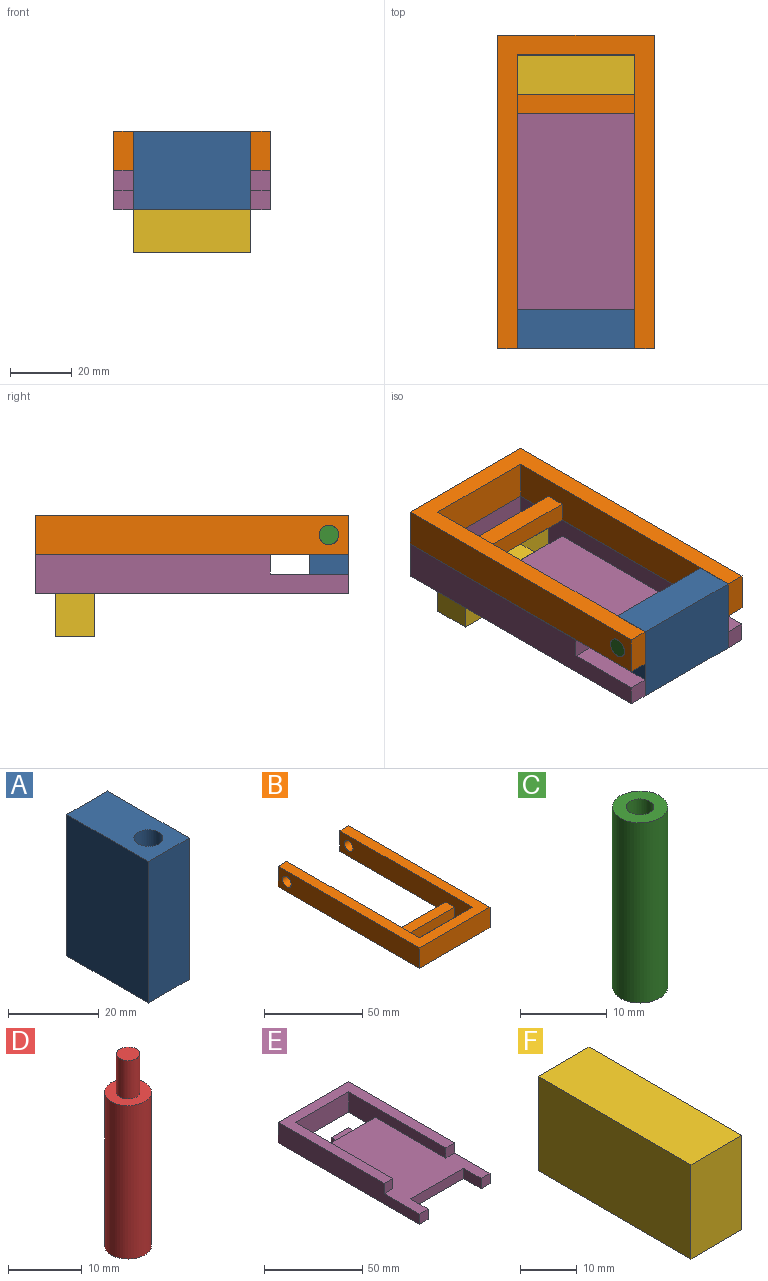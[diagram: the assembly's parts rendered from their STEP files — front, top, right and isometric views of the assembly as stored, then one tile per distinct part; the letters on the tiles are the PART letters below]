
ASSEMBLY  parts=6 mates=5
PART A: 7 faces, bbox 12.7x25.4x38.1 mm
  f0: plane 25.4x12.7mm, normal (0,0,-1), area 290.9mm2, adj f1,f3,f4,f5,f6
  f1: plane 38.1x25.4mm, normal (-1,0,0), area 967.7mm2, adj f0,f2,f4,f5
  f2: plane 25.4x12.7mm, normal (0,0,1), area 290.9mm2, adj f1,f3,f4,f5,f6
  f3: plane 38.1x25.4mm, normal (1,0,0), area 967.7mm2, adj f0,f2,f4,f5
  f4: plane 38.1x12.7mm, normal (0,1,0), area 483.9mm2, adj f0,f1,f2,f3
  f5: plane 38.1x12.7mm, normal (0,-1,0), area 483.9mm2, adj f0,f1,f2,f3
  f6: cylinder r=3.17mm len=38.1mm, axis (0,0,1), area 760.1mm2, adj f0,f2
PART B: 15 faces, bbox 50.8x101.6x12.7 mm
  f0: plane 95.25x12.7mm, normal (-1,0,0), area 1137.7mm2, adj f1,f7,f8,f9,f11,f12,f13,f14
  f1: plane 12.7x6.35mm, normal (0,1,0), area 80.6mm2, adj f0,f2,f8,f9
  f2: plane 101.6x12.7mm, normal (1,0,0), area 1258.7mm2, adj f1,f3,f8,f9,f11
  f3: plane 50.8x12.7mm, normal (0,-1,0), area 645.2mm2, adj f2,f4,f8,f9
  f4: plane 101.6x12.7mm, normal (-1,0,0), area 1258.7mm2, adj f3,f5,f8,f9,f10
  f5: plane 12.7x6.35mm, normal (0,1,0), area 80.6mm2, adj f4,f6,f8,f9
  f6: plane 95.25x12.7mm, normal (1,0,0), area 1137.7mm2, adj f5,f7,f8,f9,f10,f12,f13,f14
  f7: plane 38.1x12.7mm, normal (0,1,0), area 483.9mm2, adj f0,f6,f8,f9
  f8: plane 101.6x50.8mm, normal (0,0,-1), area 1774.2mm2, adj f0,f1,f2,f3,f4,f5,f6,f7
  f9: plane 101.6x50.8mm, normal (0,0,1), area 1532.3mm2, adj f0,f1,f2,f3,f4,f5,f6,f7
  f10: cylinder r=3.17mm len=6.35mm, axis (1,0,0), area 126.7mm2, adj f4,f6
  f11: cylinder r=3.17mm len=6.35mm, axis (1,0,0), area 126.7mm2, adj f0,f2
  f12: plane 38.1x6.35mm, normal (0,0,1), area 241.9mm2, adj f0,f6,f13,f14
  f13: plane 38.1x6.35mm, normal (0,1,0), area 241.9mm2, adj f0,f6,f8,f12
  f14: plane 38.1x6.35mm, normal (0,-1,0), area 241.9mm2, adj f0,f6,f8,f12
PART C: 5 faces, bbox 6.4x6.4x25.4 mm
  f0: cylinder r=3.17mm len=25.4mm, axis (0,0,-1), area 506.7mm2, adj f1,f2
  f1: plane 6.35x6.35mm, normal (0,0,1), area 23.8mm2, adj f0,f3
  f2: plane 6.35x6.35mm, normal (0,0,-1), area 31.7mm2, adj f0
  f3: cylinder r=1.59mm len=6.35mm, axis (0,0,1), area 63.3mm2, adj f1,f4
  f4: plane 3.18x3.18mm, normal (0,0,1), area 7.9mm2, adj f3
PART D: 5 faces, bbox 6.4x6.4x31.8 mm
  f0: cylinder r=3.17mm len=25.4mm, axis (0,0,-1), area 506.7mm2, adj f1,f2
  f1: plane 6.35x6.35mm, normal (0,0,1), area 23.8mm2, adj f0,f3
  f2: plane 6.35x6.35mm, normal (0,0,-1), area 31.7mm2, adj f0
  f3: cylinder r=1.59mm len=6.35mm, axis (0,0,-1), area 63.3mm2, adj f1,f4
  f4: plane 3.18x3.18mm, normal (0,0,1), area 7.9mm2, adj f3
PART E: 21 faces, bbox 50.8x101.6x12.7 mm
  f0: plane 12.7x3.18mm, normal (0,1,0), area 40.3mm2, adj f1,f2,f19,f20
  f1: plane 12.7x6.35mm, normal (0,0,1), area 80.6mm2, adj f0,f18,f19,f20
  f2: plane 101.6x50.8mm, normal (0,0,-1), area 4032.3mm2, adj f0,f3,f5,f6,f7,f8,f10,f11
  f3: plane 6.35x6.35mm, normal (0,-1,0), area 40.3mm2, adj f2,f7,f14,f16
  f4: plane 76.2x50.8mm, normal (0,0,1), area 1209.7mm2, adj f5,f7,f8,f9,f10,f11,f12,f13
  f5: plane 101.6x12.7mm, normal (-1,0,0), area 1129mm2, adj f2,f4,f6,f8,f13,f14
  f6: plane 6.35x6.35mm, normal (0,-1,0), area 40.3mm2, adj f2,f5,f14,f15
  f7: plane 101.6x12.7mm, normal (1,0,0), area 1129mm2, adj f2,f3,f4,f8,f9,f14
  f8: plane 50.8x12.7mm, normal (0,1,0), area 645.2mm2, adj f2,f4,f5,f7
  f9: plane 6.35x6.35mm, normal (0,-1,0), area 40.3mm2, adj f4,f7,f10,f14
  f10: plane 69.85x12.7mm, normal (-1,0,0), area 564.5mm2, adj f2,f4,f9,f11,f14,f18
  f11: plane 38.1x12.7mm, normal (0,-1,0), area 483.9mm2, adj f2,f4,f10,f12
  f12: plane 69.85x12.7mm, normal (1,0,0), area 564.5mm2, adj f2,f4,f11,f13,f14,f18
  f13: plane 6.35x6.35mm, normal (0,-1,0), area 40.3mm2, adj f4,f5,f12,f14
  f14: plane 76.2x50.8mm, normal (0,0,1), area 2741.9mm2, adj f3,f5,f6,f7,f9,f10,f12,f13
  f15: plane 12.7x6.35mm, normal (1,0,0), area 80.6mm2, adj f2,f6,f14,f17
  f16: plane 12.7x6.35mm, normal (-1,0,0), area 80.6mm2, adj f2,f3,f14,f17
  f17: plane 38.1x6.35mm, normal (0,-1,0), area 241.9mm2, adj f2,f14,f15,f16
  f18: plane 38.1x6.35mm, normal (0,1,0), area 201.6mm2, adj f1,f2,f10,f12,f14,f19,f20
  f19: plane 6.35x3.18mm, normal (-1,0,0), area 20.2mm2, adj f0,f1,f2,f18
  f20: plane 6.35x3.18mm, normal (1,0,0), area 20.2mm2, adj f0,f1,f2,f18
PART F: 10 faces, bbox 19.1x38.1x20.3 mm
  f0: plane 12.7x3.18mm, normal (1,0,0), area 40.3mm2, adj f1,f2,f8,f9
  f1: plane 12.7x6.35mm, normal (0,0,1), area 80.6mm2, adj f0,f6,f8,f9
  f2: plane 38.1x19.05mm, normal (0,0,-1), area 564.5mm2, adj f0,f3,f4,f5,f6,f8,f9
  f3: plane 38.1x20.32mm, normal (-1,0,0), area 774.2mm2, adj f2,f4,f5,f7
  f4: plane 20.32x12.7mm, normal (0,-1,0), area 258.1mm2, adj f2,f3,f6,f7
  f5: plane 20.32x12.7mm, normal (0,1,0), area 258.1mm2, adj f2,f3,f6,f7
  f6: plane 38.1x20.32mm, normal (1,0,0), area 733.9mm2, adj f1,f2,f4,f5,f7,f8,f9
  f7: plane 38.1x12.7mm, normal (0,0,1), area 483.9mm2, adj f3,f4,f5,f6
  f8: plane 6.35x3.18mm, normal (0,1,0), area 20.2mm2, adj f0,f1,f2,f6
  f9: plane 6.35x3.18mm, normal (0,-1,0), area 20.2mm2, adj f0,f1,f2,f6
PLACE A rot(axis=(-0.58,0.58,-0.58),120deg) t=(-13.21,-178.74,-1.07)mm
PLACE B rot(axis=(0,0,1),180deg) t=(2.48,-53.69,-37.12)mm
PLACE C rot(axis=(0.71,0,0.71),180deg) t=(-19.56,-185.76,-33.55)mm
PLACE D rot(axis=(-0.71,0,0.71),180deg) t=(31.24,-185.76,-28)mm
PLACE E rot(axis=(0.35,0.74,-0.57),0deg) t=(13.48,-147.95,-37.12)mm
PLACE F rot(axis=(0.71,-0.71,0),180deg) t=(17.56,-117.25,-30.77)mm
MATE planar E.f1 <-> F.f1  axis (0,0,1) through (5.84,-94.44,-33.95)mm
MATE planar E.f17 <-> A.f1  axis (0,-1,0) through (5.84,-161.11,-37.12)mm
MATE planar C.f0 <-> D.f0  axis (1,0,0) through (5.84,-167.46,-18.07)mm
MATE revolute A.f6 <-> D.f0  axis (1,0,0) through (5.84,-167.46,-18.07)mm
MATE planar B.f10 <-> C.f0  axis (-1,0,0) through (-19.56,-167.46,-18.07)mm
